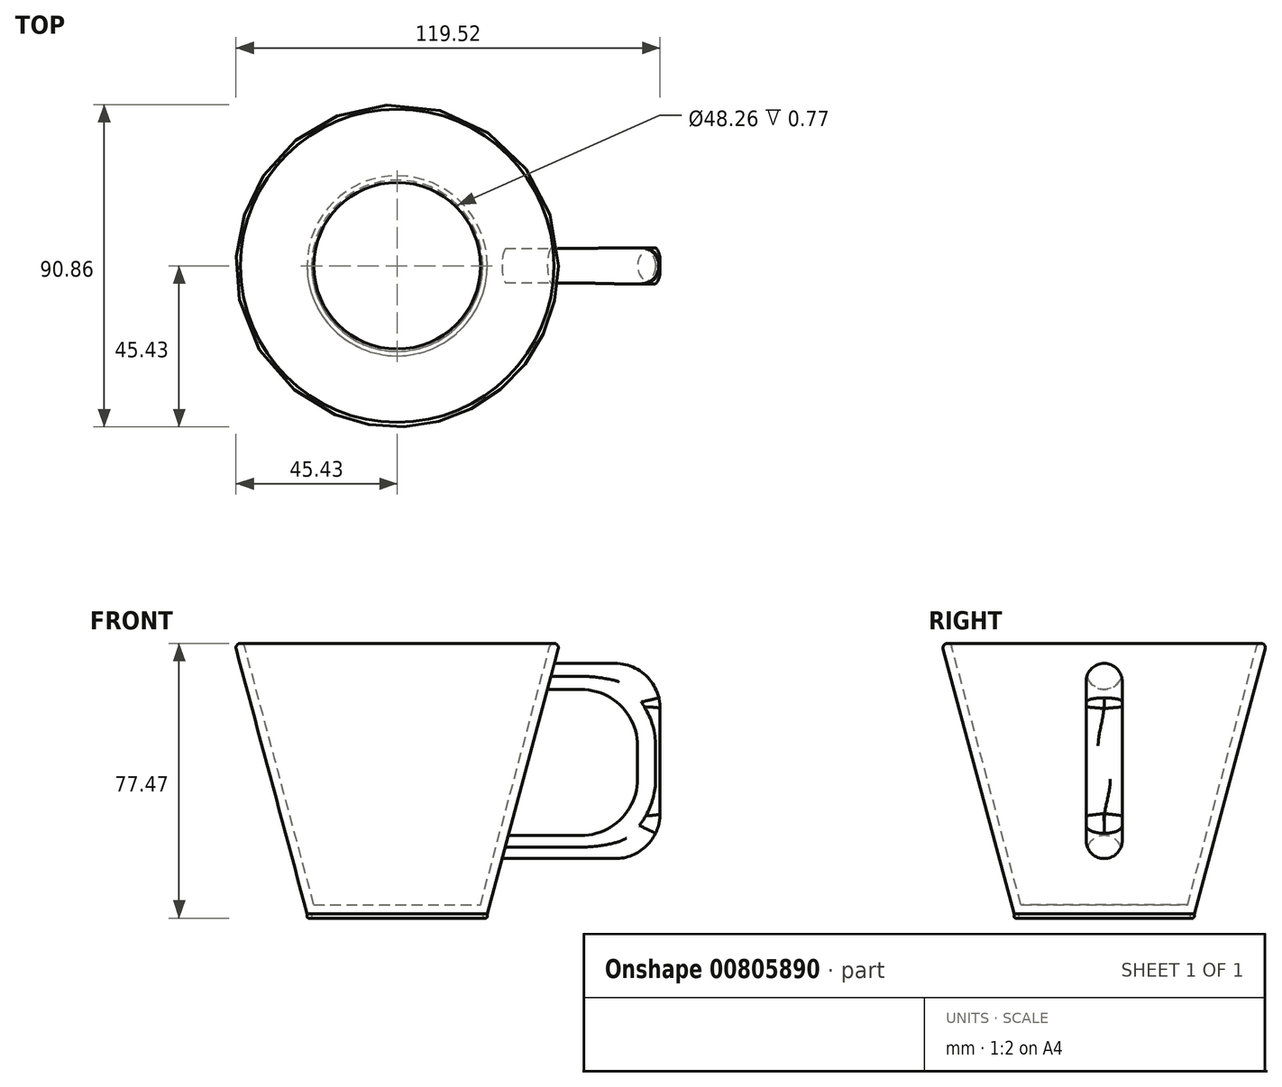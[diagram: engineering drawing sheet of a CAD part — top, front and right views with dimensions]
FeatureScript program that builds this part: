
annotation { "Feature Type Name" : "Feature", "Feature Type Description" : "" }
export const myFeature = defineFeature(function(context is Context, id is Id, definition is map)
    precondition{}
    {
        {
            var Q0;
            Q0=qCreatedBy(makeId("Front.planeOp"),FACE);
            var sketch = newSketch(context, id + "F0", { "sketchPlane" : qUnion([Q0])});
            skLineSegment(sketch, "E0", {"start": v(0, 0) * mm, "end": v(25.4, 0) * mm});
            skLineSegment(sketch, "E1", {"start": v(25.4, 0) * mm, "end": v(25.4, 76.2) * mm, "construction": true});
            skLineSegment(sketch, "E2", {"start": v(25.4, 76.2) * mm, "end": v(70.75, 76.2) * mm, "construction": true});
            skLineSegment(sketch, "E3", {"start": v(25.4, 0) * mm, "end": v(45.82, 76.2) * mm});
            skLineSegment(sketch, "E4", {"start": v(0, 0) * mm, "end": v(0, 76.2) * mm});
            skLineSegment(sketch, "E5", {"start": v(45.82, 76.2) * mm, "end": v(0, 76.2) * mm});
            skLineSegment(sketch, "E6", {"start": v(31.3, 22.03) * mm, "end": v(51.8, 22.03) * mm});
            skLineSegment(sketch, "E7", {"start": v(67.74, 37.96) * mm, "end": v(67.74, 47.28) * mm});
            skLineSegment(sketch, "E8", {"start": v(51.8, 63.2) * mm, "end": v(42.34, 63.2) * mm});
            skPoint(sketch, "E9.visualSharp", {"position": v(67.74, 63.2) * mm});
            skArc(sketch, "E9.filletArc", {"start": v(67.74, 47.28) * mm, "mid": v(63.07, 58.54) * mm, "end": v(51.8, 63.2) * mm});
            skPoint(sketch, "E10.visualSharp", {"position": v(67.74, 22.03) * mm});
            skArc(sketch, "E10.filletArc", {"start": v(51.8, 22.03) * mm, "mid": v(63.07, 26.7) * mm, "end": v(67.74, 37.96) * mm});
            skLineSegment(sketch, "E11", {"start": v(29.56, 15.5) * mm, "end": v(51.8, 15.5) * mm});
            skLineSegment(sketch, "E12", {"start": v(51.8, 15.5) * mm, "end": v(61.39, 15.5) * mm});
            skLineSegment(sketch, "E13", {"start": v(44.3, 70.55) * mm, "end": v(51.8, 70.55) * mm});
            skLineSegment(sketch, "E14", {"start": v(51.8, 70.55) * mm, "end": v(61.39, 70.55) * mm});
            skLineSegment(sketch, "E15", {"start": v(74.09, 57.85) * mm, "end": v(74.09, 28.2) * mm});
            skPoint(sketch, "E16.orphan", {"position": v(96.37, 70.55) * mm});
            skPoint(sketch, "E17.visualSharp", {"position": v(74.09, 70.55) * mm});
            skArc(sketch, "E17.filletArc", {"start": v(74.09, 57.85) * mm, "mid": v(70.37, 66.83) * mm, "end": v(61.39, 70.55) * mm});
            skPoint(sketch, "E18.visualSharp", {"position": v(74.09, 15.5) * mm});
            skArc(sketch, "E18.filletArc", {"start": v(61.39, 15.5) * mm, "mid": v(70.37, 19.23) * mm, "end": v(74.09, 28.2) * mm});
            skLineSegment(sketch, "E19", {"start": v(25.4, 0) * mm, "end": v(25.4, -1.27) * mm});
            skLineSegment(sketch, "E20", {"start": v(25.4, -1.27) * mm, "end": v(24.13, -1.27) * mm});
            skLineSegment(sketch, "E21", {"start": v(24.13, -1.27) * mm, "end": v(24.13, 0) * mm});
            skSolve(sketch);
        }
        {
            var Q0;
            {var subQ4=sQuery(id+"F0.wireOp",EDGE,"E0");Q0=makeQuery(id+"F0.imprint","IMPRINT",FACE,{"disambiguationData":[TD([[makeQuery(id+"F0.imprint","IMPRINT",EDGE,{"derivedFrom":subQ4}),1.0]])]});}
            var Q1;
            {var subQ0=sQuery(id+"F0.wireOp",EDGE,"E19");Q1=makeQuery(id+"F0.imprint","IMPRINT",FACE,{"disambiguationData":[TD([[makeQuery(id+"F0.imprint","IMPRINT",EDGE,{"derivedFrom":subQ0}),-1.0]])]});}
            var Q2;
            Q2=sQuery(id+"F0.wireOp",EDGE,"E4");
            revolve(context, id + "F1", {"surfaceOperationType" : NewSurfaceOperationType.NEW, "entities" : qUnion([Q0, Q1]), "axis" : qUnion([Q2]), "revolveType" : RevolveType.FULL});
        }
        {
            var Q0;
            Q0=makeQuery(id+"F1.opRevolve","SWEPT_FACE",FACE,{"disambiguationData":[OSD([sQuery(id+"F0.wireOp",EDGE,"E5")])]});
            shell(context, id + "F2", {"entities" : qUnion([Q0]), "thickness" : 2.5 * mm});
        }
        {
            var Q0;
            {var subQ2=sQuery(id+"F0.wireOp",EDGE,"E6");Q0=makeQuery(id+"F0.imprint","IMPRINT",FACE,{"disambiguationData":[TD([[makeQuery(id+"F0.imprint","IMPRINT",EDGE,{"derivedFrom":subQ2}),-1.0]])]});}
            extrude(context, id + "F3", {"entities" : qUnion([Q0]), "endBound" : BoundingType.SYMMETRIC, "depth" : 10.16 * mm, "offsetDistance" : 25.4 * mm});
        }
        {
            var Q0;
            Q0=makeQuery(id+"F3.opExtrude","CAP_EDGE",EDGE,{"disambiguationData":[OSD([sQuery(id+"F0.wireOp",EDGE,"E10.filletArc")])],"isStart":false});
            var Q1;
            Q1=makeQuery(id+"F3.opExtrude","CAP_EDGE",EDGE,{"disambiguationData":[OSD([sQuery(id+"F0.wireOp",EDGE,"E10.filletArc")])],"isStart":true});
            fillet(context, id + "F4", {"entities" : qUnion([Q0, Q1]), "radius" : 5.08 * mm, "tangentPropagation" : true, "allowEdgeOverflow" : false});
        }
        {
            var Q0;
            Q0=makeQuery(id+"F3.opExtrude","CAP_EDGE",EDGE,{"disambiguationData":[OSD([sQuery(id+"F0.wireOp",EDGE,"E18.filletArc")])],"isStart":true});
            var Q1;
            Q1=makeQuery(id+"F3.opExtrude","CAP_EDGE",EDGE,{"disambiguationData":[OSD([sQuery(id+"F0.wireOp",EDGE,"E18.filletArc")])],"isStart":false});
            fillet(context, id + "F5", {"entities" : qUnion([Q0, Q1]), "radius" : 5.08 * mm, "tangentPropagation" : true, "allowEdgeOverflow" : false});
        }
        {
            var Q0;
            Q0=makeQuery(id+"F1.opRevolve","SWEPT_EDGE",EDGE,{"disambiguationData":[OSD([sQuery(id+"F0.wireOp",EDGE,"E3"),sQuery(id+"F0.wireOp",EDGE,"E5")])]});
            fillet(context, id + "F6", {"entities" : qUnion([Q0]), "radius" : 1.27 * mm, "tangentPropagation" : true, "allowEdgeOverflow" : false});
        }
        {
            var Q0;
            Q0=makeQuery(id+"F2.opShell","OFFSET_EDGE",EDGE,{"disambiguationData":[OSD([sQuery(id+"F0.wireOp",EDGE,"E3"),sQuery(id+"F0.wireOp",EDGE,"E5")])]});
            fillet(context, id + "F7", {"entities" : qUnion([Q0]), "radius" : 1.27 * mm, "tangentPropagation" : true, "allowEdgeOverflow" : false});
        }
        {
            var Q0;
            Q0=makeQuery(id+"F1.opRevolve","SWEPT_EDGE",EDGE,{"disambiguationData":[OSD([sQuery(id+"F0.wireOp",EDGE,"E19"),sQuery(id+"F0.wireOp",EDGE,"E20")])]});
            fillet(context, id + "F8", {"entities" : qUnion([Q0]), "radius" : .5 * mm, "tangentPropagation" : true, "allowEdgeOverflow" : false});
        }
        {
            var Q0;
            Q0=makeQuery(id+"F1.opRevolve","SWEPT_EDGE",EDGE,{"disambiguationData":[OSD([sQuery(id+"F0.wireOp",EDGE,"E20"),sQuery(id+"F0.wireOp",EDGE,"E21")])]});
            fillet(context, id + "F9", {"entities" : qUnion([Q0]), "radius" : .5 * mm, "tangentPropagation" : true, "allowEdgeOverflow" : false});
        }
    });
